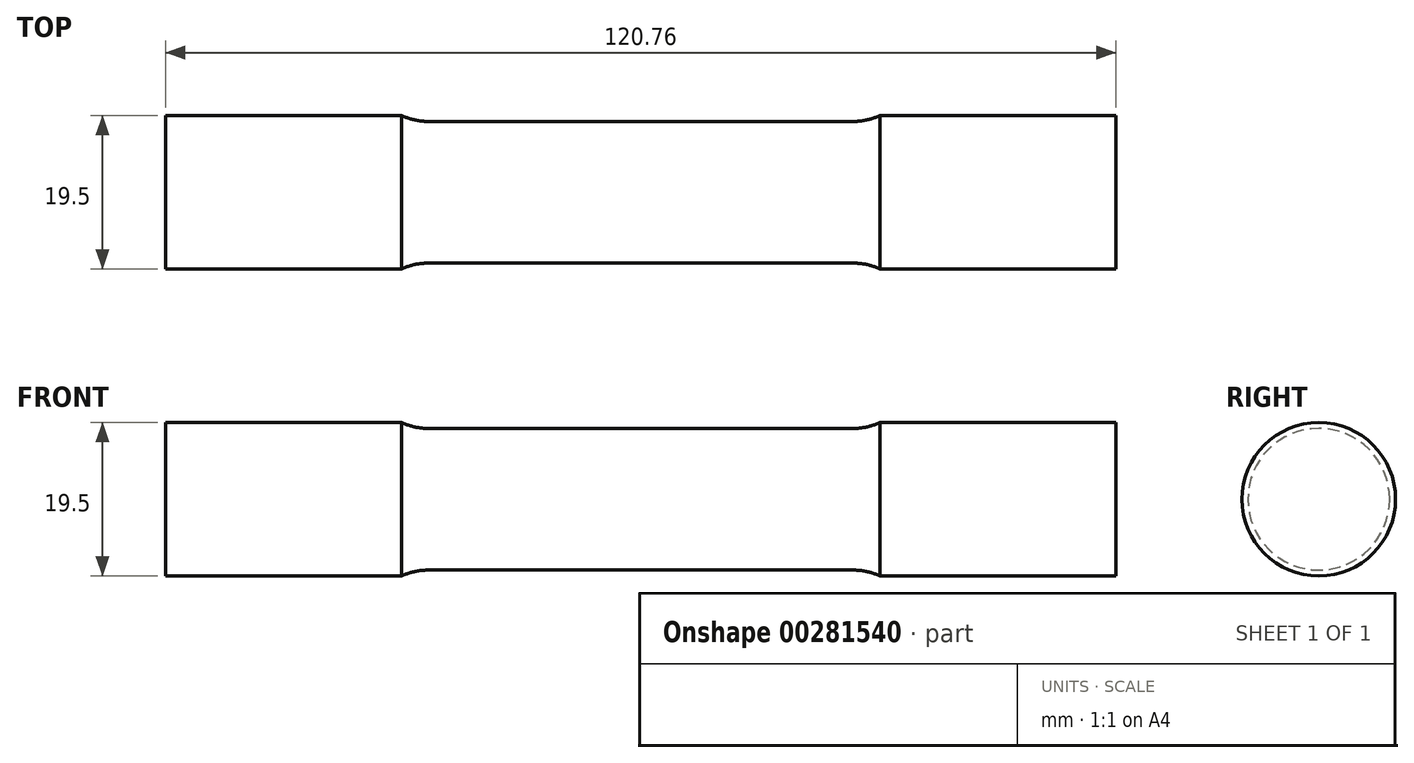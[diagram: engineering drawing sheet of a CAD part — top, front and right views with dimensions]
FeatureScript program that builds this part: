
annotation { "Feature Type Name" : "Feature", "Feature Type Description" : "" }
export const myFeature = defineFeature(function(context is Context, id is Id, definition is map)
    precondition{}
    {
        {
            var Q0;
            Q0=qCreatedBy(makeId("Front.planeOp"),FACE);
            var sketch = newSketch(context, id + "F0", { "sketchPlane" : qUnion([Q0])});
            skLineSegment(sketch, "E0", {"start": v(0, 9) * mm, "end": v(27, 9) * mm});
            skLineSegment(sketch, "E1", {"start": v(30.39, 9.75) * mm, "end": v(60.38, 9.75) * mm});
            skLineSegment(sketch, "E2", {"start": v(60.38, 9.75) * mm, "end": v(60.38, 0) * mm});
            skLineSegment(sketch, "E3.MirrorCS", {"start": v(0, 9) * mm, "end": v(-27, 9) * mm});
            skLineSegment(sketch, "E4.MirrorCS", {"start": v(-60.38, 9.75) * mm, "end": v(-60.38, 0) * mm});
            skLineSegment(sketch, "E5.MirrorCS", {"start": v(-30.39, 9.75) * mm, "end": v(-60.38, 9.75) * mm});
            skLineSegment(sketch, "E6", {"start": v(-60.38, 0) * mm, "end": v(60.38, 0) * mm});
            skArc(sketch, "E7", {"start": v(-30.39, 9.75) * mm, "mid": v(-28.74, 9.2) * mm, "end": v(-27, 9) * mm});
            skArc(sketch, "E8", {"start": v(27, 9) * mm, "mid": v(28.74, 9.2) * mm, "end": v(30.39, 9.75) * mm});
            skSolve(sketch);
        }
        {
            var Q0;
            Q0 = qSketchRegion(id + "F0", true);
            var Q1;
            Q1=sQuery(id+"F0.wireOp",EDGE,"E6");
            revolve(context, id + "F1", {"entities" : qUnion([Q0]), "axis" : qUnion([Q1]), "revolveType" : RevolveType.FULL});
        }
    });
